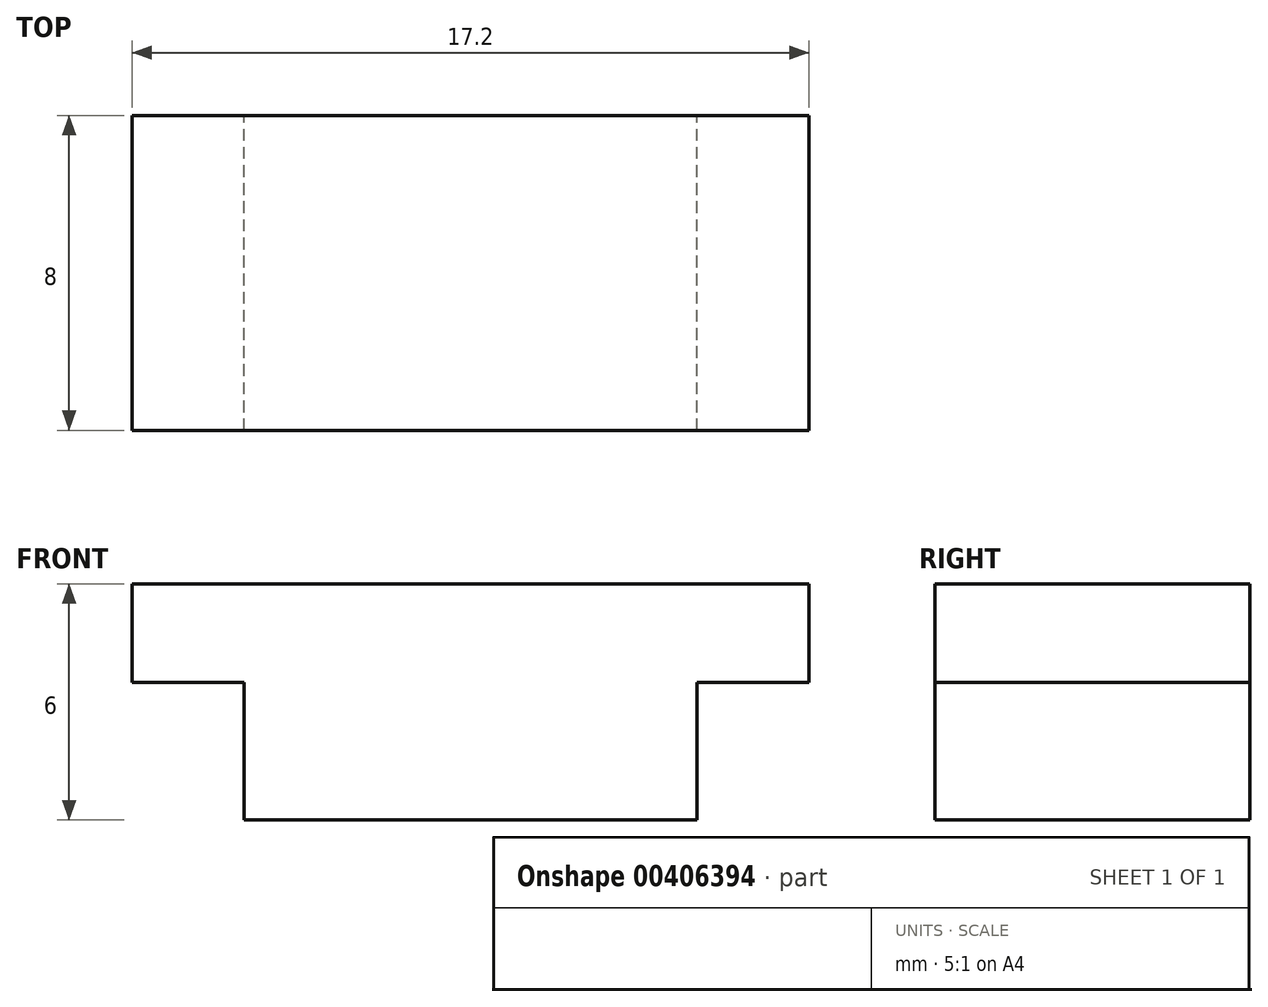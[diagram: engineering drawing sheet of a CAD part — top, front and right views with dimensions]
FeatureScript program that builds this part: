
annotation { "Feature Type Name" : "Feature", "Feature Type Description" : "" }
export const myFeature = defineFeature(function(context is Context, id is Id, definition is map)
    precondition{}
    {
        {
            var Q0;
            Q0=qCreatedBy(makeId("Front.planeOp"),FACE);
            var sketch = newSketch(context, id + "F0", { "sketchPlane" : qUnion([Q0])});
            skLineSegment(sketch, "E0", {"start": v(0, 0) * mm, "end": v(-5.75, 0) * mm});
            skLineSegment(sketch, "E1", {"start": v(-5.75, 0) * mm, "end": v(-5.75, 3.5) * mm});
            skLineSegment(sketch, "E2", {"start": v(-5.75, 3.5) * mm, "end": v(-8.6, 3.5) * mm});
            skLineSegment(sketch, "E3", {"start": v(-8.6, 3.5) * mm, "end": v(-8.6, 6) * mm});
            skLineSegment(sketch, "E4", {"start": v(-8.6, 6) * mm, "end": v(8.6, 6) * mm});
            skLineSegment(sketch, "E5", {"start": v(8.6, 6) * mm, "end": v(8.6, 3.5) * mm});
            skLineSegment(sketch, "E6", {"start": v(8.6, 3.5) * mm, "end": v(5.75, 3.5) * mm});
            skLineSegment(sketch, "E7", {"start": v(5.75, 3.5) * mm, "end": v(5.75, 0) * mm});
            skLineSegment(sketch, "E8", {"start": v(5.75, 0) * mm, "end": v(0, 0) * mm});
            skSolve(sketch);
        }
        {
            var Q0;
            Q0 = qSketchRegion(id + "F0", true);
            extrude(context, id + "F1", {"entities" : qUnion([Q0]), "depth" : 8 * mm});
        }
    });
